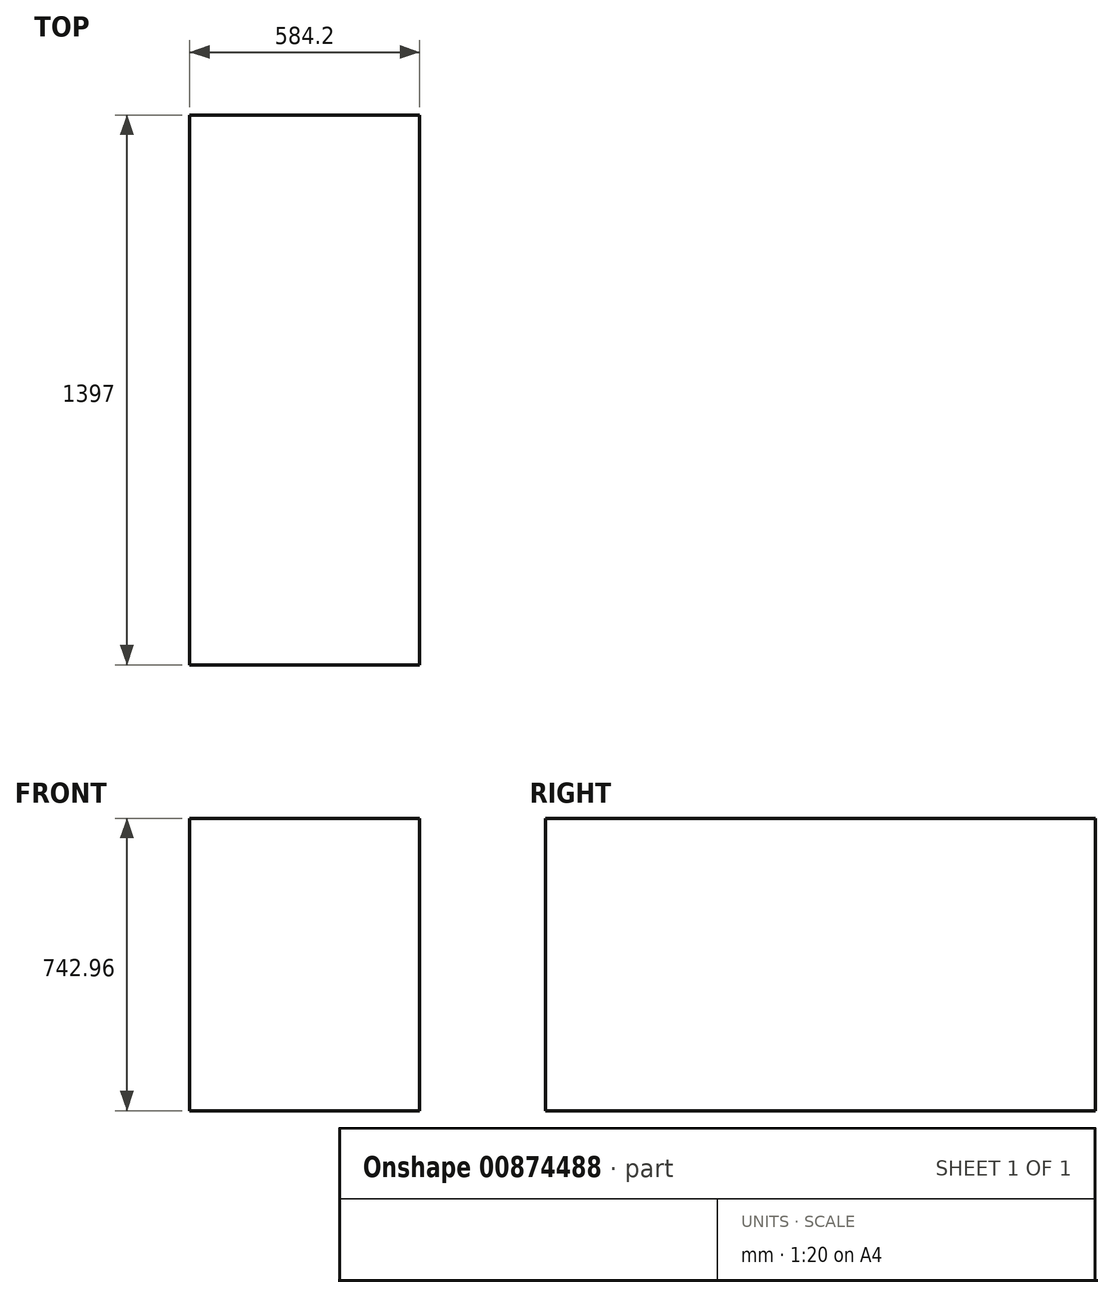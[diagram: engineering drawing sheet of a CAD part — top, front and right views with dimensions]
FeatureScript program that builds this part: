
annotation { "Feature Type Name" : "Feature", "Feature Type Description" : "" }
export const myFeature = defineFeature(function(context is Context, id is Id, definition is map)
    precondition{}
    {
        {
            var Q0;
            Q0=qCreatedBy(makeId("Front.planeOp"),FACE);
            var sketch = newSketch(context, id + "F0", { "sketchPlane" : qUnion([Q0])});
            skLineSegment(sketch, "E0.bottom", {"start": v(-292.1, 371.48) * mm, "end": v(292.1, 371.48) * mm});
            skLineSegment(sketch, "E0.top", {"start": v(-292.1, -371.48) * mm, "end": v(292.1, -371.48) * mm});
            skLineSegment(sketch, "E0.left", {"start": v(-292.1, 371.48) * mm, "end": v(-292.1, -371.48) * mm});
            skLineSegment(sketch, "E0.right", {"start": v(292.1, 371.48) * mm, "end": v(292.1, -371.48) * mm});
            skPoint(sketch, "E0.middle", {"position": v(0, 0) * mm});
            skSolve(sketch);
        }
        {
            var Q0;
            Q0=makeQuery(id+"F0.imprint","IMPRINT",FACE,{"disambiguationData":[TD([[makeQuery(id+"F0.imprint","IMPRINT",EDGE,{"derivedFrom":sQuery(id+"F0.wireOp",EDGE,"E0.bottom")}),-1.0]])]});
            extrude(context, id + "F1", {"entities" : qUnion([Q0]), "depth" : 1397 * mm, "offsetDistance" : 25.4 * mm});
        }
    });
